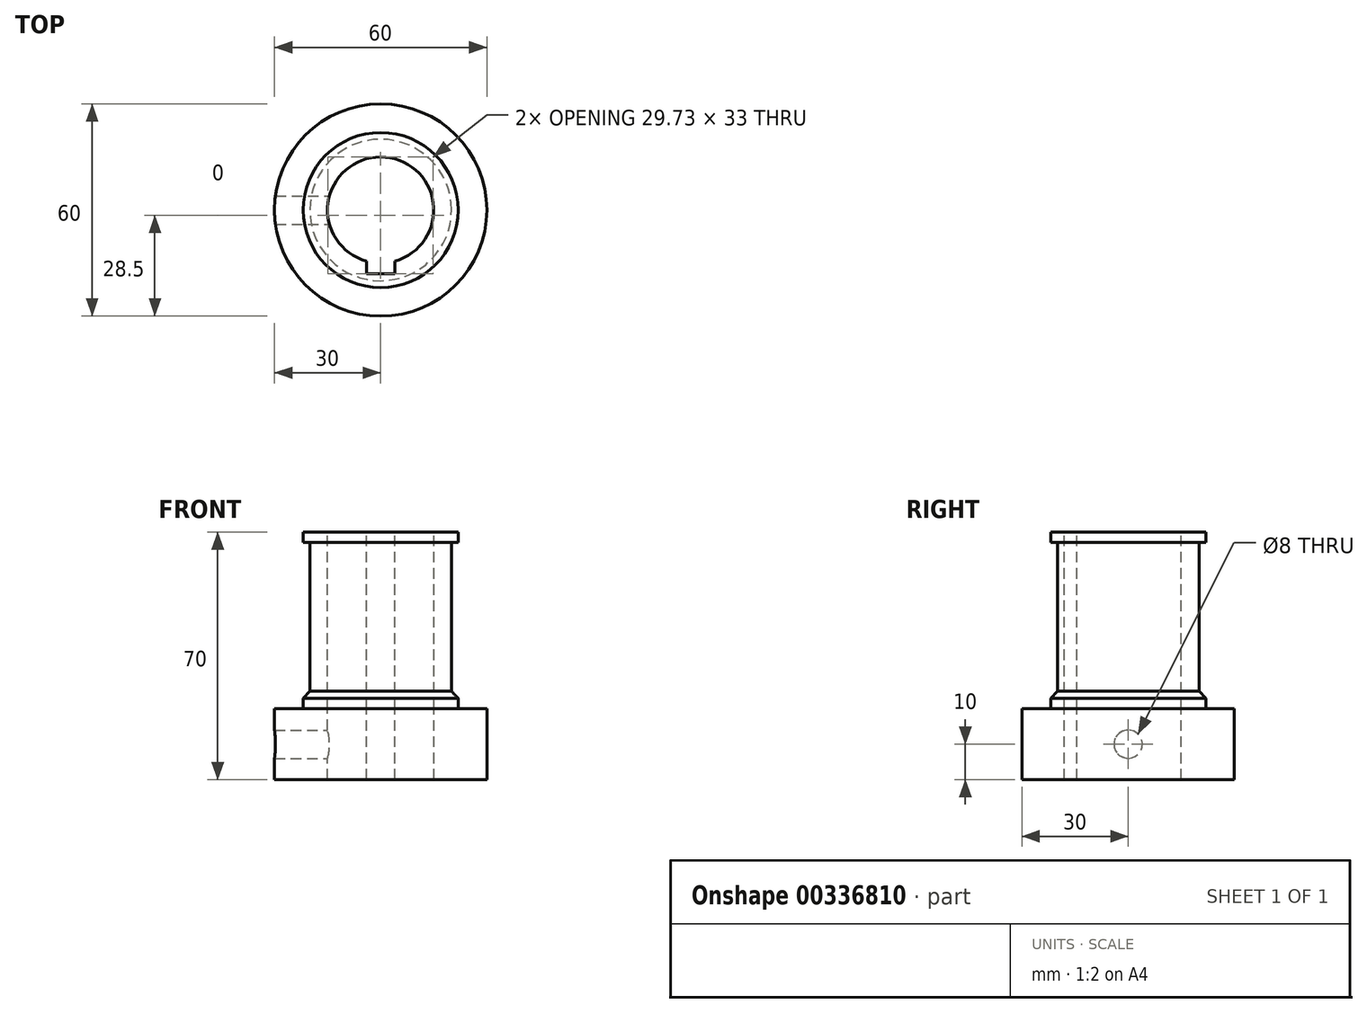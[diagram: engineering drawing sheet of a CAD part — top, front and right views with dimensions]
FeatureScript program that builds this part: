
annotation { "Feature Type Name" : "Feature", "Feature Type Description" : "" }
export const myFeature = defineFeature(function(context is Context, id is Id, definition is map)
    precondition{}
    {
        {
            var Q0;
            Q0=qCreatedBy(makeId("Top.planeOp"),FACE);
            var sketch = newSketch(context, id + "F0", { "sketchPlane" : qUnion([Q0])});
            skCircle(sketch, "E0", {"center": v(0, 0) * mm, "radius": 30 * mm});
            skSolve(sketch);
        }
        {
            var Q0;
            Q0 = qSketchRegion(id + "F0", true);
            extrude(context, id + "F1", {"entities" : qUnion([Q0]), "depth" : 20 * mm});
        }
        {
            var Q0;
            Q0=makeQuery(id+"F1.opExtrude","CAP_FACE",FACE,{"disambiguationData":[OSD([sQuery(id+"F0.wireOp",EDGE,"E0")])],"isStart":false});
            cPlane(context, id + "F2", {"entities" : qUnion([Q0]), "cplaneType" : CPlaneType.OFFSET, "offset" : 0 * mm, "width" : 150 * mm, "height" : 150 * mm});
        }
        {
            var Q0;
            Q0=qCreatedBy(id+"F2.planeOp",FACE);
            var sketch = newSketch(context, id + "F3", { "sketchPlane" : qUnion([Q0])});
            skCircle(sketch, "E1", {"center": v(0, 0) * mm, "radius": 21.9 * mm});
            skSolve(sketch);
        }
        {
            var Q0;
            Q0=makeQuery(id+"F3.imprint","IMPRINT",FACE,{"disambiguationData":[TD([[makeQuery(id+"F3.imprint","IMPRINT",EDGE,{"derivedFrom":sQuery(id+"F3.wireOp",EDGE,"E1")}),1.0]])]});
            var Q1;
            Q1=sQuery(id+"F3.wireOp",EDGE,"E1");
            extrude(context, id + "F4", {"entities" : qUnion([Q0]), "surfaceEntities" : qUnion([Q1]), "depth" : 3 * mm});
        }
        {
            var Q0;
            Q0=makeQuery(id+"F4.opExtrude","CAP_FACE",FACE,{"disambiguationData":[OSD([sQuery(id+"F3.wireOp",EDGE,"E1")])],"isStart":false});
            cPlane(context, id + "F5", {"entities" : qUnion([Q0]), "cplaneType" : CPlaneType.OFFSET, "offset" : 0 * mm, "width" : 150 * mm, "height" : 150 * mm});
        }
        {
            var Q0;
            Q0=qCreatedBy(id+"F5.planeOp",FACE);
            var sketch = newSketch(context, id + "F6", { "sketchPlane" : qUnion([Q0])});
            skCircle(sketch, "E2", {"center": v(0, 0) * mm, "radius": 21.9 * mm});
            skSolve(sketch);
        }
        {
            var Q0;
            Q0 = qSketchRegion(id + "F6", true);
            extrude(context, id + "F7", {"entities" : qUnion([Q0]), "operationType" : NewBodyOperationType.ADD, "depth" : 2 * mm});
        }
        {
            var Q0;
            Q0=makeQuery(id+"F7.opExtrude","CAP_FACE",FACE,{"disambiguationData":[OSD([sQuery(id+"F6.wireOp",EDGE,"E2")])],"isStart":false});
            cPlane(context, id + "F8", {"entities" : qUnion([Q0]), "cplaneType" : CPlaneType.OFFSET, "offset" : 0 * mm, "width" : 150 * mm, "height" : 150 * mm});
        }
        {
            var Q0;
            Q0=qCreatedBy(id+"F8.planeOp",FACE);
            var sketch = newSketch(context, id + "F9", { "sketchPlane" : qUnion([Q0])});
            skCircle(sketch, "E3", {"center": v(0, 0) * mm, "radius": 20 * mm});
            skSolve(sketch);
        }
        {
            var Q0;
            Q0 = qSketchRegion(id + "F9", true);
            extrude(context, id + "F10", {"entities" : qUnion([Q0]), "operationType" : NewBodyOperationType.ADD, "depth" : 42 * mm});
        }
        {
            var Q0;
            Q0=makeQuery(id+"F10.opExtrude","CAP_FACE",FACE,{"disambiguationData":[OSD([sQuery(id+"F9.wireOp",EDGE,"E3")])],"isStart":false});
            cPlane(context, id + "F11", {"entities" : qUnion([Q0]), "cplaneType" : CPlaneType.OFFSET, "offset" : 0 * mm, "width" : 150 * mm, "height" : 150 * mm});
        }
        {
            var Q0;
            Q0=qCreatedBy(id+"F11.planeOp",FACE);
            var sketch = newSketch(context, id + "F12", { "sketchPlane" : qUnion([Q0])});
            skCircle(sketch, "E4", {"center": v(0, 0) * mm, "radius": 21.9 * mm});
            skSolve(sketch);
        }
        {
            var Q0;
            Q0 = qSketchRegion(id + "F12", true);
            extrude(context, id + "F13", {"entities" : qUnion([Q0]), "operationType" : NewBodyOperationType.ADD, "depth" : 3 * mm});
        }
        {
            var Q0;
            Q0=makeQuery(id+"F13.opExtrude","CAP_FACE",FACE,{"disambiguationData":[OSD([sQuery(id+"F12.wireOp",EDGE,"E4")])],"isStart":false});
            cPlane(context, id + "F14", {"entities" : qUnion([Q0]), "cplaneType" : CPlaneType.OFFSET, "offset" : 0 * mm, "width" : 150 * mm, "height" : 150 * mm});
        }
        {
            var Q0;
            Q0=qCreatedBy(makeId("Right.planeOp"),FACE);
            var sketch = newSketch(context, id + "F15", { "sketchPlane" : qUnion([Q0])});
            skCircle(sketch, "E5", {"center": v(0, 10) * mm, "radius": 4 * mm});
            skSolve(sketch);
        }
        {
            var Q0;
            Q0 = qSketchRegion(id + "F15", true);
            extrude(context, id + "F16", {"entities" : qUnion([Q0]), "operationType" : NewBodyOperationType.REMOVE, "oppositeDirection" : true, "depth" : 63.4 * mm});
        }
        {
            var Q0;
            Q0=qCreatedBy(id+"F14.planeOp",FACE);
            var sketch = newSketch(context, id + "F17", { "sketchPlane" : qUnion([Q0])});
            skArc(sketch, "E6", {"start": v(4, -14.46) * mm, "mid": v(0, 15) * mm, "end": v(-4, -14.46) * mm});
            skLineSegment(sketch, "E7", {"start": v(4, -14.46) * mm, "end": v(4, -18) * mm});
            skLineSegment(sketch, "E8", {"start": v(4, -18) * mm, "end": v(-4, -18) * mm});
            skLineSegment(sketch, "E9", {"start": v(-4, -18) * mm, "end": v(-4, -14.46) * mm});
            skSolve(sketch);
        }
        {
            var Q0;
            Q0 = qSketchRegion(id + "F17", true);
            extrude(context, id + "F18", {"entities" : qUnion([Q0]), "operationType" : NewBodyOperationType.REMOVE, "oppositeDirection" : true, "depth" : 171 * mm});
        }
        {
            var Q0;
            Q0=makeQuery(id+"F7.opExtrude","CAP_EDGE",EDGE,{"disambiguationData":[OSD([sQuery(id+"F6.wireOp",EDGE,"E2")])],"isStart":false});
            chamfer(context, id + "F19", {"entities" : qUnion([Q0]), "chamferType" : ChamferType.TWO_OFFSETS, "width1" : 1.9 * mm, "oppositeDirection" : false, "width2" : 2 * mm, "tangentPropagation" : true});
        }
    });
